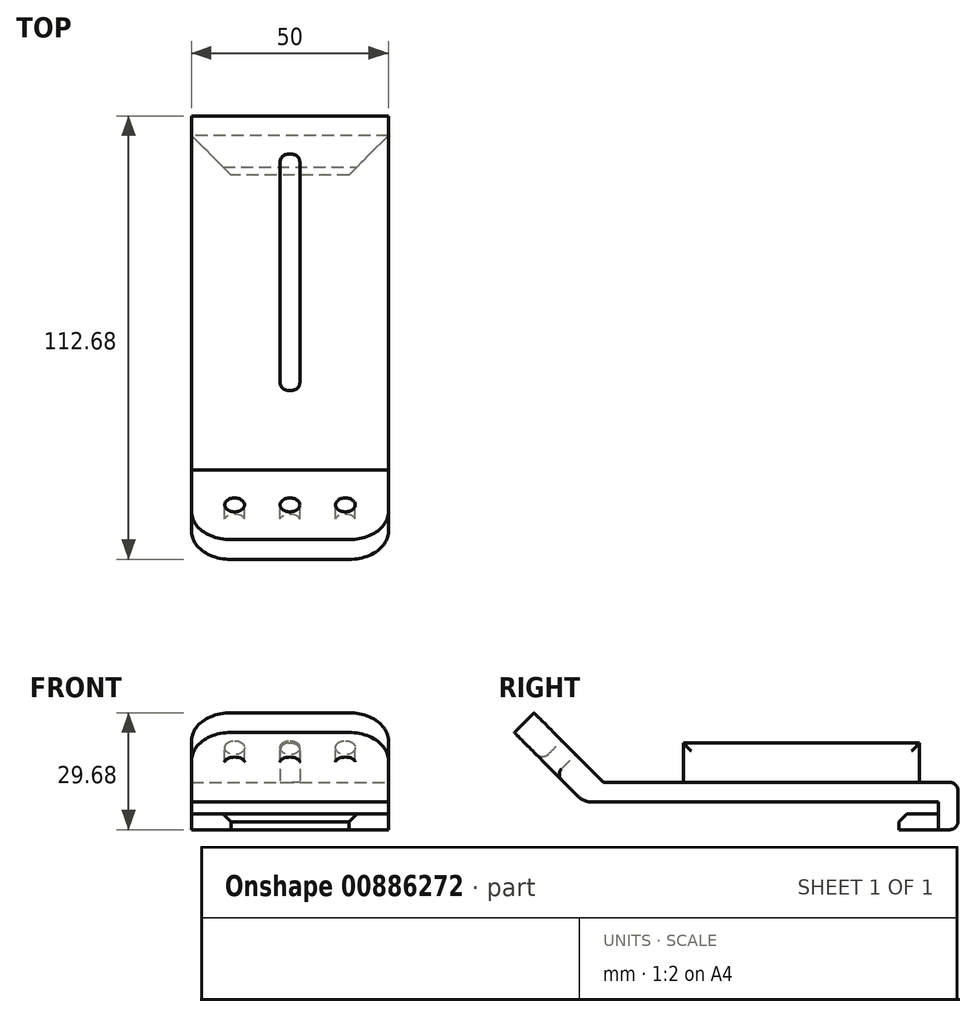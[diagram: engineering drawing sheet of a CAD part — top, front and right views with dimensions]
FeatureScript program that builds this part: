
annotation { "Feature Type Name" : "Feature", "Feature Type Description" : "" }
export const myFeature = defineFeature(function(context is Context, id is Id, definition is map)
    precondition{}
    {
        {
            var Q0;
            Q0=qCreatedBy(makeId("Front.planeOp"),FACE);
            var sketch = newSketch(context, id + "F0", { "sketchPlane" : qUnion([Q0])});
            skLineSegment(sketch, "E0.bottom", {"start": v(0, 0) * mm, "end": v(25, 0) * mm});
            skLineSegment(sketch, "E0.top", {"start": v(0, 5) * mm, "end": v(25, 5) * mm});
            skLineSegment(sketch, "E0.right", {"start": v(25, 0) * mm, "end": v(25, 5) * mm});
            skLineSegment(sketch, "E1.MirrorCS", {"start": v(0, 0) * mm, "end": v(-25, 0) * mm});
            skLineSegment(sketch, "E2.MirrorCS", {"start": v(-25, 0) * mm, "end": v(-25, 5) * mm});
            skLineSegment(sketch, "E3.MirrorCS", {"start": v(0, 5) * mm, "end": v(-25, 5) * mm});
            skSolve(sketch);
        }
        {
            var Q0;
            Q0 = qSketchRegion(id + "F0", true);
            extrude(context, id + "F1", {"entities" : qUnion([Q0]), "depth" : 90 * mm, "offsetDistance" : 25 * mm});
        }
        {
            var Q0;
            Q0=makeQuery(id+"F1.opExtrude","CAP_FACE",FACE,{"disambiguationData":[OSD([sQuery(id+"F0.wireOp",EDGE,"E0.bottom"),sQuery(id+"F0.wireOp",EDGE,"E0.top"),sQuery(id+"F0.wireOp",EDGE,"E0.right"),sQuery(id+"F0.wireOp",EDGE,"E1.MirrorCS"),sQuery(id+"F0.wireOp",EDGE,"E2.MirrorCS"),sQuery(id+"F0.wireOp",EDGE,"E3.MirrorCS")])],"isStart":true});
            var sketch = newSketch(context, id + "F2", { "sketchPlane" : qUnion([Q0])});
            skLineSegment(sketch, "E4.bottom", {"start": v(-25, 5) * mm, "end": v(25, 5) * mm});
            skLineSegment(sketch, "E4.top", {"start": v(-25, 0) * mm, "end": v(25, 0) * mm});
            skLineSegment(sketch, "E4.left", {"start": v(-25, 5) * mm, "end": v(-25, 0) * mm});
            skLineSegment(sketch, "E4.right", {"start": v(25, 5) * mm, "end": v(25, 0) * mm});
            skLineSegment(sketch, "E5.top", {"start": v(-25, -3) * mm, "end": v(25, -3) * mm});
            skLineSegment(sketch, "E5.left", {"start": v(-25, 0) * mm, "end": v(-25, -3) * mm});
            skLineSegment(sketch, "E5.right", {"start": v(25, 0) * mm, "end": v(25, -3) * mm});
            skLineSegment(sketch, "E6.top", {"start": v(-25, -7) * mm, "end": v(25, -7) * mm});
            skLineSegment(sketch, "E6.left", {"start": v(-25, -3) * mm, "end": v(-25, -7) * mm});
            skLineSegment(sketch, "E6.right", {"start": v(25, -3) * mm, "end": v(25, -7) * mm});
            skSolve(sketch);
        }
        {
            var Q0;
            Q0 = qSketchRegion(id + "F2", true);
            extrude(context, id + "F3", {"entities" : qUnion([Q0]), "operationType" : NewBodyOperationType.ADD, "depth" : 5 * mm, "offsetDistance" : 25 * mm});
        }
        {
            var Q0;
            Q0=makeQuery(id+"F2.imprint","IMPRINT",FACE,{"disambiguationData":[TD([[makeQuery(id+"F2.imprint","IMPRINT",EDGE,{"derivedFrom":sQuery(id+"F2.wireOp",EDGE,"E5.top")}),-1.0]])]});
            extrude(context, id + "F4", {"entities" : qUnion([Q0]), "operationType" : NewBodyOperationType.ADD, "oppositeDirection" : true, "depth" : 10 * mm, "offsetDistance" : 25 * mm});
        }
        {
            var Q0;
            Q0=makeQuery(id+"F4.opExtrude","CAP_EDGE",EDGE,{"disambiguationData":[OSD([sQuery(id+"F2.wireOp",EDGE,"E6.right")])],"isStart":false});
            var Q1;
            Q1=makeQuery(id+"F4.opExtrude","CAP_EDGE",EDGE,{"disambiguationData":[OSD([sQuery(id+"F2.wireOp",EDGE,"E6.left")])],"isStart":false});
            chamfer(context, id + "F5", {"entities" : qUnion([Q0, Q1]), "width" : 10 * mm, "tangentPropagation" : true});
        }
        {
            var Q0;
            Q0=makeQuery(id+"F1.opExtrude","CAP_EDGE",EDGE,{"disambiguationData":[OSD([sQuery(id+"F0.wireOp",EDGE,"E0.top"),sQuery(id+"F0.wireOp",EDGE,"E3.MirrorCS")])],"isStart":false});
            chamfer(context, id + "F6", {"entities" : qUnion([Q0]), "width" : 5 * mm, "tangentPropagation" : true});
        }
        {
            var Q0;
            Q0=makeQuery(id+"F6.opChamfer","BLEND_FACE",FACE,{"disambiguationData":[OSD([sQuery(id+"F0.wireOp",EDGE,"E0.top"),sQuery(id+"F0.wireOp",EDGE,"E3.MirrorCS")])]});
            extrude(context, id + "F7", {"entities" : qUnion([Q0]), "operationType" : NewBodyOperationType.ADD, "depth" : 25 * mm, "offsetDistance" : 25 * mm});
        }
        {
            var Q0;
            Q0=makeQuery(id+"F7.opExtrude","SWEPT_FACE",FACE,{"disambiguationData":[OSD([sQuery(id+"F0.wireOp",EDGE,"E0.top"),sQuery(id+"F0.wireOp",EDGE,"E3.MirrorCS"),sQuery(id+"F2.wireOp",EDGE,"E4.bottom")])]});
            var sketch = newSketch(context, id + "F8", { "sketchPlane" : qUnion([Q0])});
            skLineSegment(sketch, "E7", {"start": v(-25, 76.14) * mm, "end": v(25, 76.14) * mm});
            skCircle(sketch, "E8", {"center": v(-14.07, 76.14) * mm, "radius": 2.5 * mm});
            skCircle(sketch, "E9", {"center": v(0, 76.14) * mm, "radius": 2.5 * mm});
            skCircle(sketch, "E10.MirrorC", {"center": v(14.07, 76.14) * mm, "radius": 2.5 * mm});
            skSolve(sketch);
        }
        {
            var Q0;
            Q0 = qSketchRegion(id + "F8", true);
            extrude(context, id + "F9", {"entities" : qUnion([Q0]), "operationType" : NewBodyOperationType.REMOVE, "oppositeDirection" : true, "depth" : 25 * mm, "offsetDistance" : 25 * mm});
        }
        {
            var Q0;
            Q0=makeQuery(id+"F3.boolean.opBoolean","MERGE",FACE,{"derivedFrom":[makeQuery(id+"F1.opExtrude","SWEPT_FACE",FACE,{"disambiguationData":[OSD([sQuery(id+"F0.wireOp",EDGE,"E0.top"),sQuery(id+"F0.wireOp",EDGE,"E3.MirrorCS")])]}),makeQuery(id+"F3.opExtrude","SWEPT_FACE",FACE,{"disambiguationData":[OSD([sQuery(id+"F2.wireOp",EDGE,"E4.bottom")])]})]});
            var sketch = newSketch(context, id + "F10", { "sketchPlane" : qUnion([Q0])});
            skLineSegment(sketch, "E11.bottom", {"start": v(0, -4.74) * mm, "end": v(2.5, -4.74) * mm});
            skLineSegment(sketch, "E11.top", {"start": v(0, -64.74) * mm, "end": v(2.5, -64.74) * mm});
            skLineSegment(sketch, "E11.left", {"start": v(0, -4.74) * mm, "end": v(0, -64.74) * mm});
            skLineSegment(sketch, "E11.right", {"start": v(2.5, -4.74) * mm, "end": v(2.5, -64.74) * mm});
            skLineSegment(sketch, "E12.MirrorCS", {"start": v(0, -4.74) * mm, "end": v(-2.5, -4.74) * mm});
            skLineSegment(sketch, "E13.MirrorCS", {"start": v(-2.5, -4.74) * mm, "end": v(-2.5, -64.74) * mm});
            skLineSegment(sketch, "E14.MirrorCS", {"start": v(0, -64.74) * mm, "end": v(-2.5, -64.74) * mm});
            skSolve(sketch);
        }
        {
            var Q0;
            Q0 = qSketchRegion(id + "F10", true);
            extrude(context, id + "F11", {"entities" : qUnion([Q0]), "operationType" : NewBodyOperationType.ADD, "depth" : 10 * mm, "offsetDistance" : 25 * mm});
        }
        {
            var Q0;
            Q0=makeQuery(id+"F7.opExtrude","CAP_EDGE",EDGE,{"disambiguationData":[OSD([sQuery(id+"F0.wireOp",EDGE,"E0.top"),sQuery(id+"F0.wireOp",EDGE,"E2.MirrorCS"),sQuery(id+"F0.wireOp",EDGE,"E3.MirrorCS"),sQuery(id+"F2.wireOp",EDGE,"E4.right"),sQuery(id+"F2.wireOp",EDGE,"E5.right"),sQuery(id+"F2.wireOp",EDGE,"E6.right")])],"isStart":false});
            var Q1;
            Q1=makeQuery(id+"F7.opExtrude","CAP_EDGE",EDGE,{"disambiguationData":[OSD([sQuery(id+"F0.wireOp",EDGE,"E0.top"),sQuery(id+"F0.wireOp",EDGE,"E0.right"),sQuery(id+"F0.wireOp",EDGE,"E3.MirrorCS"),sQuery(id+"F2.wireOp",EDGE,"E4.left"),sQuery(id+"F2.wireOp",EDGE,"E5.left"),sQuery(id+"F2.wireOp",EDGE,"E6.left")])],"isStart":false});
            fillet(context, id + "F12", {"entities" : qUnion([Q0, Q1]), "radius" : 10 * mm, "tangentPropagation" : true, "allowEdgeOverflow" : false});
        }
        {
            var Q0;
            {var subQ0=sQuery(id+"F0.wireOp",EDGE,"E3.MirrorCS");var subQ1=sQuery(id+"F0.wireOp",EDGE,"E1.MirrorCS");var subQ2=sQuery(id+"F0.wireOp",EDGE,"E0.top");var subQ3=sQuery(id+"F0.wireOp",EDGE,"E0.bottom");Q0=makeQuery(id+"F7.boolean.opBoolean","MERGE",EDGE,{"derivedFrom":[makeQuery(id+"F6.opChamfer","BLEND_EDGE",EDGE,{"blendedFrom":[makeQuery(id+"F1.opExtrude","CAP_EDGE",EDGE,{"disambiguationData":[OSD([subQ2,subQ0])],"isStart":false}),makeQuery(id+"F1.opExtrude","SWEPT_FACE",FACE,{"disambiguationData":[OSD([subQ3,subQ1])]})],"blendedInto":[makeQuery(id+"F1.opExtrude","SWEPT_FACE",FACE,{"disambiguationData":[OSD([subQ3,subQ1])]})]}),makeQuery(id+"F7.opExtrude","CAP_EDGE",EDGE,{"disambiguationData":[OSD([subQ3,subQ2,subQ1,subQ0])],"isStart":true})]});}
            fillet(context, id + "F13", {"entities" : qUnion([Q0]), "radius" : 5 * mm, "tangentPropagation" : true, "allowEdgeOverflow" : false});
        }
        {
            var Q0;
            Q0=makeQuery(id+"F4.opExtrude","CAP_EDGE",EDGE,{"disambiguationData":[OSD([sQuery(id+"F2.wireOp",EDGE,"E5.top")])],"isStart":false});
            chamfer(context, id + "F14", {"entities" : qUnion([Q0]), "width" : 2 * mm, "tangentPropagation" : true});
        }
        {
            var Q0;
            Q0=makeQuery(id+"F11.opExtrude","SWEPT_EDGE",EDGE,{"disambiguationData":[OSD([sQuery(id+"F10.wireOp",EDGE,"E12.MirrorCS"),sQuery(id+"F10.wireOp",EDGE,"E13.MirrorCS")])]});
            var Q1;
            Q1=makeQuery(id+"F11.opExtrude","SWEPT_EDGE",EDGE,{"disambiguationData":[OSD([sQuery(id+"F10.wireOp",EDGE,"E11.bottom"),sQuery(id+"F10.wireOp",EDGE,"E11.right")])]});
            var Q2;
            Q2=makeQuery(id+"F11.opExtrude","SWEPT_EDGE",EDGE,{"disambiguationData":[OSD([sQuery(id+"F10.wireOp",EDGE,"E13.MirrorCS"),sQuery(id+"F10.wireOp",EDGE,"E14.MirrorCS")])]});
            var Q3;
            Q3=makeQuery(id+"F11.opExtrude","SWEPT_EDGE",EDGE,{"disambiguationData":[OSD([sQuery(id+"F10.wireOp",EDGE,"E11.top"),sQuery(id+"F10.wireOp",EDGE,"E11.right")])]});
            var Q4;
            Q4=makeQuery(id+"F11.opExtrude","CAP_EDGE",EDGE,{"disambiguationData":[OSD([sQuery(id+"F10.wireOp",EDGE,"E13.MirrorCS")])],"isStart":false});
            var Q5;
            Q5=makeQuery(id+"F11.opExtrude","CAP_EDGE",EDGE,{"disambiguationData":[OSD([sQuery(id+"F10.wireOp",EDGE,"E11.right")])],"isStart":false});
            fillet(context, id + "F15", {"entities" : qUnion([Q0, Q1, Q2, Q3, Q4, Q5]), "radius" : 2 * mm, "tangentPropagation" : true, "allowEdgeOverflow" : false});
        }
        {
            var Q0;
            Q0=makeQuery(id+"F3.opExtrude","CAP_EDGE",EDGE,{"disambiguationData":[OSD([sQuery(id+"F2.wireOp",EDGE,"E4.bottom")])],"isStart":false});
            var Q1;
            Q1=makeQuery(id+"F3.opExtrude","CAP_EDGE",EDGE,{"disambiguationData":[OSD([sQuery(id+"F2.wireOp",EDGE,"E6.top")])],"isStart":false});
            fillet(context, id + "F16", {"entities" : qUnion([Q0, Q1]), "radius" : 2 * mm, "tangentPropagation" : true, "allowEdgeOverflow" : false});
        }
        {
            var Q0;
            Q0=makeQuery(id+"F9.boolean.opBoolean","COPY",EDGE,{"derivedFrom":makeQuery(id+"F9.opExtrude","CAP_EDGE",EDGE,{"disambiguationData":[OSD([sQuery(id+"F8.wireOp",EDGE,"E10.MirrorC")])],"isStart":true})});
            var Q1;
            Q1=makeQuery(id+"F9.boolean.opBoolean","COPY",EDGE,{"derivedFrom":makeQuery(id+"F9.opExtrude","CAP_EDGE",EDGE,{"disambiguationData":[OSD([sQuery(id+"F8.wireOp",EDGE,"E9")])],"isStart":true})});
            var Q2;
            Q2=makeQuery(id+"F9.boolean.opBoolean","COPY",EDGE,{"derivedFrom":makeQuery(id+"F9.opExtrude","CAP_EDGE",EDGE,{"disambiguationData":[OSD([sQuery(id+"F8.wireOp",EDGE,"E8")])],"isStart":true})});
            var Q3;
            Q3=makeQuery(id+"F9.boolean.opBoolean","INTERSECT",EDGE,{"derivedFrom":[makeQuery(id+"F7.opExtrude","SWEPT_FACE",FACE,{"disambiguationData":[OSD([sQuery(id+"F0.wireOp",EDGE,"E0.bottom"),sQuery(id+"F0.wireOp",EDGE,"E0.top"),sQuery(id+"F0.wireOp",EDGE,"E1.MirrorCS"),sQuery(id+"F0.wireOp",EDGE,"E3.MirrorCS")])]}),makeQuery(id+"F9.opExtrude","SWEPT_FACE",FACE,{"disambiguationData":[OSD([sQuery(id+"F8.wireOp",EDGE,"E10.MirrorC")])]})]});
            var Q4;
            Q4=makeQuery(id+"F9.boolean.opBoolean","INTERSECT",EDGE,{"derivedFrom":[makeQuery(id+"F7.opExtrude","SWEPT_FACE",FACE,{"disambiguationData":[OSD([sQuery(id+"F0.wireOp",EDGE,"E0.bottom"),sQuery(id+"F0.wireOp",EDGE,"E0.top"),sQuery(id+"F0.wireOp",EDGE,"E1.MirrorCS"),sQuery(id+"F0.wireOp",EDGE,"E3.MirrorCS")])]}),makeQuery(id+"F9.opExtrude","SWEPT_FACE",FACE,{"disambiguationData":[OSD([sQuery(id+"F8.wireOp",EDGE,"E9")])]})]});
            var Q5;
            Q5=makeQuery(id+"F9.boolean.opBoolean","INTERSECT",EDGE,{"derivedFrom":[makeQuery(id+"F7.opExtrude","SWEPT_FACE",FACE,{"disambiguationData":[OSD([sQuery(id+"F0.wireOp",EDGE,"E0.bottom"),sQuery(id+"F0.wireOp",EDGE,"E0.top"),sQuery(id+"F0.wireOp",EDGE,"E1.MirrorCS"),sQuery(id+"F0.wireOp",EDGE,"E3.MirrorCS")])]}),makeQuery(id+"F9.opExtrude","SWEPT_FACE",FACE,{"disambiguationData":[OSD([sQuery(id+"F8.wireOp",EDGE,"E8")])]})]});
            fillet(context, id + "F17", {"entities" : qUnion([Q0, Q1, Q2, Q3, Q4, Q5]), "radius" : 2 * mm, "tangentPropagation" : true, "allowEdgeOverflow" : false});
        }
    });
